# Revit family: 1Electronics_Community-Point-Source_Biamp_Loudspeaker_IP6_1122WR
name_source: partatom
category: Communication Devices
units: mm (PartAtom-declared; Revit-internal decimal feet)

## family parameters
Cut with Voids When Loaded = No
Host = Face
Maintain Annotation Orientation = No
OmniClass Number = 23.85.10.11.14.14.14
Part Type = Normal
Room Calculation Point = No
Round Connector Dimension = Use Diameter
Shared = No

## types (1)
- Please download type catalogue!
    Continuous Power Handling  Nominal Impedance = LF - 63V, 500W @ 8 ohms (2000W peak); HF - 24V, 75W @ 8 ohms (300W peak)
    Default Elevation = 4' - 0"
    Depth = 1' - 5 11/16"
    Description = IP6-1122WR Medium Power 12-Inch Two-Way Weather-Resistant Installation Loudspeaker
    Environmental = IP55W per IEC 60529
    Equalized Maximum SPL = Peak: 127 dB - Continuous: 121 dB
    Equalized Sensitivity = 1W: 93 dB - 2.83V: 93 dB
    Gril Material = Biamp - Plastic - Black(Grid)
    Height = 2' - 4"
    Housing Material = Biamp - Plastic - Black
    Input Connection = Sealed Gland Nut with 12ft (3.6m) 14 Ga. SJOW cable
    Manufacturer = Biamp
    Mounting Points = 15
    Operating Environment = Weather-Resistant Outdoor
    Operating Mode = Passive or Biamp with DSP
    Product Page URL = https://www.biamp.com
    Product data url = https://www.bimobject.com
    Recommended Amplifiers = LF - 500W - 1000W @ 8 ohms, (63V - 89V); HF - 75W - 150W @ 8 ohms (24V - 35V)
    Shipping Weight = 74.00 lbf
    Transducers = LF 1 x 12 (305mm) ferrite driver, 2.5 (64mm) voice coil, inherently
weather resistant cone; HF 1 x 1.4 (36mm) exit, 3 (76mm) voice coil, hybrid titanium polyimide diaphragm, ferrite compression driver
    URL = https://www.biamp.com
    Weight = 65.00 lbf
    Width = 1' - 2 1/2"

## geometry (parser evidence)
native form markers: Sweep x2
no freeform markers — native parametric forms only
